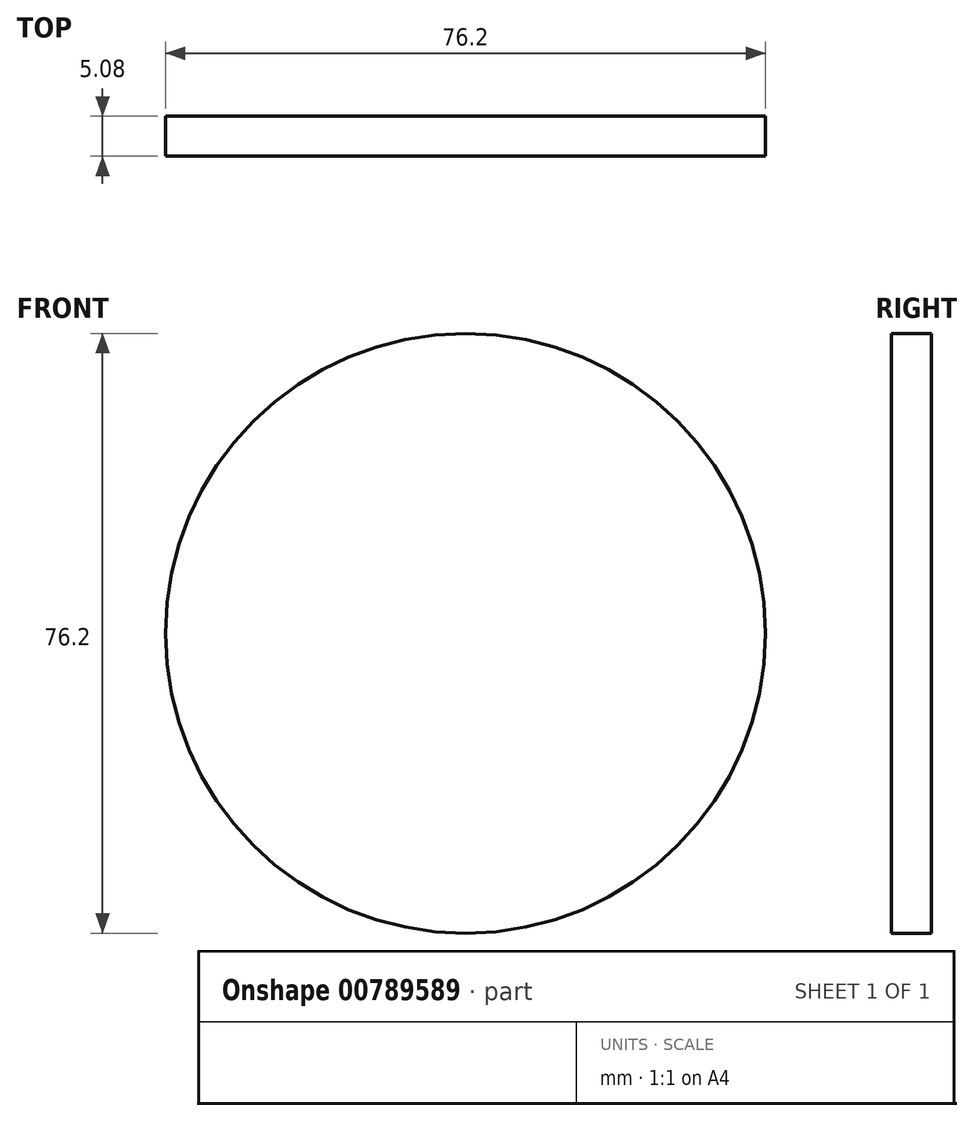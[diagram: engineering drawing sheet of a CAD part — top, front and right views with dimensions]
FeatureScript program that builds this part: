
annotation { "Feature Type Name" : "Feature", "Feature Type Description" : "" }
export const myFeature = defineFeature(function(context is Context, id is Id, definition is map)
    precondition{}
    {
        {
            var Q0;
            Q0=qCreatedBy(makeId("Front.planeOp"),FACE);
            var sketch = newSketch(context, id + "F0", { "sketchPlane" : qUnion([Q0])});
            skCircle(sketch, "E0", {"center": v(0, 0) * mm, "radius": 38.1 * mm});
            skSolve(sketch);
        }
        {
            var Q0;
            Q0=makeQuery(id+"F0.imprint","IMPRINT",FACE,{"disambiguationData":[TD([[makeQuery(id+"F0.imprint","IMPRINT",EDGE,{"derivedFrom":sQuery(id+"F0.wireOp",EDGE,"E0")}),1.0]])]});
            extrude(context, id + "F1", {"entities" : qUnion([Q0]), "depth" : 5.08 * mm, "offsetDistance" : 25.4 * mm});
        }
    });
